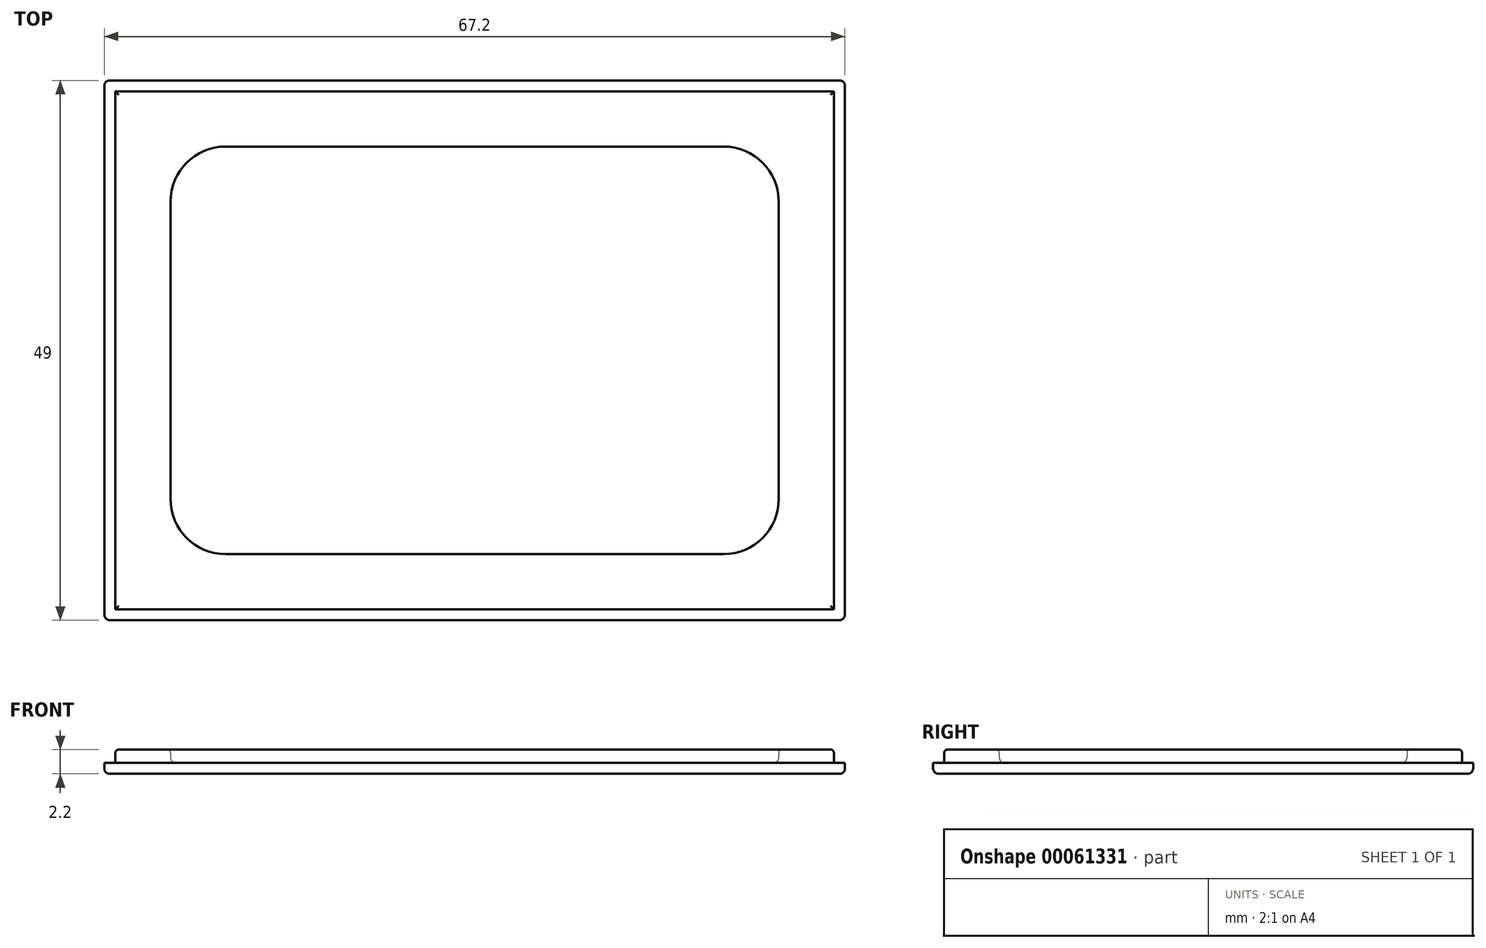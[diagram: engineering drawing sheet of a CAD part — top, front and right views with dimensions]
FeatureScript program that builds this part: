
annotation { "Feature Type Name" : "Feature", "Feature Type Description" : "" }
export const myFeature = defineFeature(function(context is Context, id is Id, definition is map)
    precondition{}
    {
        {
            var Q0;
            Q0=qCreatedBy(makeId("Top.planeOp"),FACE);
            var sketch = newSketch(context, id + "F0", { "sketchPlane" : qUnion([Q0])});
            skLineSegment(sketch, "E0.bottom", {"start": v(-25.22, 29.05) * mm, "end": v(41.98, 29.05) * mm});
            skLineSegment(sketch, "E0.top", {"start": v(-25.22, -19.95) * mm, "end": v(41.98, -19.95) * mm});
            skLineSegment(sketch, "E0.left", {"start": v(-25.22, 29.05) * mm, "end": v(-25.22, -19.95) * mm});
            skLineSegment(sketch, "E0.right", {"start": v(41.98, 29.05) * mm, "end": v(41.98, -19.95) * mm});
            skLineSegment(sketch, "E1.0", {"start": v(-24.22, 28.05) * mm, "end": v(40.98, 28.05) * mm});
            skLineSegment(sketch, "E1.1", {"start": v(-24.22, 28.05) * mm, "end": v(-24.22, -18.95) * mm});
            skLineSegment(sketch, "E1.2", {"start": v(-24.22, -18.95) * mm, "end": v(40.98, -18.95) * mm});
            skLineSegment(sketch, "E1.3", {"start": v(40.98, 28.05) * mm, "end": v(40.98, -18.95) * mm});
            skLineSegment(sketch, "E2.bottom", {"start": v(32.98, 28.05) * mm, "end": v(40.98, 28.05) * mm});
            skLineSegment(sketch, "E2.right", {"start": v(40.98, 28.05) * mm, "end": v(40.98, 20.05) * mm});
            skLineSegment(sketch, "E3.top", {"start": v(40.98, -18.95) * mm, "end": v(32.98, -18.95) * mm});
            skLineSegment(sketch, "E3.left", {"start": v(40.98, -10.95) * mm, "end": v(40.98, -18.95) * mm});
            skLineSegment(sketch, "E4.bottom", {"start": v(-16.22, 28.05) * mm, "end": v(-24.22, 28.05) * mm});
            skLineSegment(sketch, "E4.right", {"start": v(-24.22, 28.05) * mm, "end": v(-24.22, 20.05) * mm});
            skLineSegment(sketch, "E5.top", {"start": v(-24.22, -18.95) * mm, "end": v(-16.22, -18.95) * mm});
            skLineSegment(sketch, "E5.left", {"start": v(-24.22, -10.95) * mm, "end": v(-24.22, -18.95) * mm});
            skLineSegment(sketch, "E6.0", {"start": v(-14.22, 23.05) * mm, "end": v(30.98, 23.05) * mm});
            skLineSegment(sketch, "E7.0", {"start": v(35.98, 18.05) * mm, "end": v(35.98, -8.95) * mm});
            skLineSegment(sketch, "E7.1", {"start": v(-14.22, -13.95) * mm, "end": v(30.98, -13.95) * mm});
            skLineSegment(sketch, "E7.2", {"start": v(-19.22, 18.05) * mm, "end": v(-19.22, -8.95) * mm});
            skArc(sketch, "E8.filletArc", {"start": v(-14.22, 23.05) * mm, "mid": v(-17.76, 21.59) * mm, "end": v(-19.22, 18.05) * mm});
            skArc(sketch, "E9.filletArc", {"start": v(35.98, 18.05) * mm, "mid": v(34.51, 21.59) * mm, "end": v(30.98, 23.05) * mm});
            skPoint(sketch, "E10.visualSharp", {"position": v(-19.22, -13.95) * mm});
            skArc(sketch, "E10.filletArc", {"start": v(-19.22, -8.95) * mm, "mid": v(-17.76, -12.49) * mm, "end": v(-14.22, -13.95) * mm});
            skPoint(sketch, "E11.visualSharp", {"position": v(35.98, -13.95) * mm});
            skArc(sketch, "E11.filletArc", {"start": v(30.98, -13.95) * mm, "mid": v(34.51, -12.49) * mm, "end": v(35.98, -8.95) * mm});
            skSolve(sketch);
        }
        {
            var Q0;
            Q0=makeQuery(id+"F0.imprint","IMPRINT",FACE,{"disambiguationData":[TD([[makeQuery(id+"F0.imprint","IMPRINT",EDGE,{"derivedFrom":sQuery(id+"F0.wireOp",EDGE,"E6.0")}),-1.0]])]});
            var Q1;
            Q1=makeQuery(id+"F0.imprint","IMPRINT",FACE,{"disambiguationData":[TD([[makeQuery(id+"F0.imprint","IMPRINT",EDGE,{"derivedFrom":sQuery(id+"F0.wireOp",EDGE,"E0.bottom")}),-1.0]])]});
            var Q2;
            Q2=makeQuery(id+"F0.imprint","IMPRINT",FACE,{"disambiguationData":[TD([[makeQuery(id+"F0.imprint","IMPRINT",EDGE,{"derivedFrom":sQuery(id+"F0.wireOp",EDGE,"E1.0")}),-1.0]])]});
            extrude(context, id + "F1", {"entities" : qUnion([Q0, Q1, Q2]), "depth" : 1 * mm});
        }
        {
            var Q0;
            Q0=makeQuery(id+"F0.imprint","IMPRINT",FACE,{"disambiguationData":[TD([[makeQuery(id+"F0.imprint","IMPRINT",EDGE,{"derivedFrom":sQuery(id+"F0.wireOp",EDGE,"E1.0")}),-1.0]])]});
            extrude(context, id + "F2", {"entities" : qUnion([Q0]), "operationType" : NewBodyOperationType.ADD, "depth" : 2.2 * mm});
        }
        {
            var Q0;
            Q0=makeQuery(id+"F1.opExtrude","CAP_FACE",FACE,{"disambiguationData":[OSD([sQuery(id+"F0.wireOp",EDGE,"E0.bottom"),sQuery(id+"F0.wireOp",EDGE,"E0.top"),sQuery(id+"F0.wireOp",EDGE,"E0.left"),sQuery(id+"F0.wireOp",EDGE,"E0.right")])],"isStart":true});
            fillet(context, id + "F3", {"entities" : qUnion([Q0]), "radius" : 0.5 * mm, "tangentPropagation" : true, "allowEdgeOverflow" : false});
        }
        {
            var Q0;
            Q0=makeQuery(id+"F2.opExtrude","CAP_FACE",FACE,{"disambiguationData":[OSD([sQuery(id+"F0.wireOp",EDGE,"E1.0"),sQuery(id+"F0.wireOp",EDGE,"E1.1"),sQuery(id+"F0.wireOp",EDGE,"E1.2"),sQuery(id+"F0.wireOp",EDGE,"E1.3"),sQuery(id+"F0.wireOp",EDGE,"E2.bottom"),sQuery(id+"F0.wireOp",EDGE,"E2.right"),sQuery(id+"F0.wireOp",EDGE,"E3.top"),sQuery(id+"F0.wireOp",EDGE,"E3.left"),sQuery(id+"F0.wireOp",EDGE,"E4.bottom"),sQuery(id+"F0.wireOp",EDGE,"E4.right"),sQuery(id+"F0.wireOp",EDGE,"E5.top"),sQuery(id+"F0.wireOp",EDGE,"E5.left"),sQuery(id+"F0.wireOp",EDGE,"E6.0"),sQuery(id+"F0.wireOp",EDGE,"E7.0"),sQuery(id+"F0.wireOp",EDGE,"E7.1"),sQuery(id+"F0.wireOp",EDGE,"E7.2"),sQuery(id+"F0.wireOp",EDGE,"E8.filletArc"),sQuery(id+"F0.wireOp",EDGE,"E9.filletArc"),sQuery(id+"F0.wireOp",EDGE,"E10.filletArc"),sQuery(id+"F0.wireOp",EDGE,"E11.filletArc")])],"isStart":false});
            fillet(context, id + "F4", {"entities" : qUnion([Q0]), "radius" : 0.3 * mm, "tangentPropagation" : true, "allowEdgeOverflow" : false});
        }
        {
            var Q0;
            Q0=makeQuery(id+"F2.opExtrude","SWEPT_EDGE",EDGE,{"disambiguationData":[OSD([sQuery(id+"F0.wireOp",EDGE,"E2.bottom"),sQuery(id+"F0.wireOp",EDGE,"E2.right")])]});
            var Q1;
            Q1=makeQuery(id+"F1.opExtrude","SWEPT_EDGE",EDGE,{"disambiguationData":[OSD([sQuery(id+"F0.wireOp",EDGE,"E0.bottom"),sQuery(id+"F0.wireOp",EDGE,"E0.right")])]});
            var Q2;
            Q2=makeQuery(id+"F2.opExtrude","SWEPT_EDGE",EDGE,{"disambiguationData":[OSD([sQuery(id+"F0.wireOp",EDGE,"E3.top"),sQuery(id+"F0.wireOp",EDGE,"E3.left")])]});
            var Q3;
            Q3=makeQuery(id+"F1.opExtrude","SWEPT_EDGE",EDGE,{"disambiguationData":[OSD([sQuery(id+"F0.wireOp",EDGE,"E0.top"),sQuery(id+"F0.wireOp",EDGE,"E0.right")])]});
            var Q4;
            Q4=makeQuery(id+"F2.opExtrude","SWEPT_EDGE",EDGE,{"disambiguationData":[OSD([sQuery(id+"F0.wireOp",EDGE,"E5.top"),sQuery(id+"F0.wireOp",EDGE,"E5.left")])]});
            var Q5;
            Q5=makeQuery(id+"F1.opExtrude","SWEPT_EDGE",EDGE,{"disambiguationData":[OSD([sQuery(id+"F0.wireOp",EDGE,"E0.top"),sQuery(id+"F0.wireOp",EDGE,"E0.left")])]});
            var Q6;
            Q6=makeQuery(id+"F2.opExtrude","SWEPT_EDGE",EDGE,{"disambiguationData":[OSD([sQuery(id+"F0.wireOp",EDGE,"E4.bottom"),sQuery(id+"F0.wireOp",EDGE,"E4.right")])]});
            var Q7;
            Q7=makeQuery(id+"F1.opExtrude","SWEPT_EDGE",EDGE,{"disambiguationData":[OSD([sQuery(id+"F0.wireOp",EDGE,"E0.bottom"),sQuery(id+"F0.wireOp",EDGE,"E0.left")])]});
            fillet(context, id + "F5", {"entities" : qUnion([Q0, Q1, Q2, Q3, Q4, Q5, Q6, Q7]), "radius" : 0.5 * mm, "tangentPropagation" : true, "allowEdgeOverflow" : false});
        }
        {
            var Q0;
            Q0=makeQuery(id+"F2.boolean.opBoolean","SPLIT",FACE,{"disambiguationData":[TD([makeQuery(id+"F2.opExtrude","SWEPT_FACE",FACE,{"disambiguationData":[OSD([sQuery(id+"F0.wireOp",EDGE,"E6.0")])]})])],"derivedFrom":makeQuery(id+"F1.opExtrude","CAP_FACE",FACE,{"disambiguationData":[OSD([sQuery(id+"F0.wireOp",EDGE,"E0.bottom"),sQuery(id+"F0.wireOp",EDGE,"E0.top"),sQuery(id+"F0.wireOp",EDGE,"E0.left"),sQuery(id+"F0.wireOp",EDGE,"E0.right")])],"isStart":false})});
            fillet(context, id + "F6", {"entities" : qUnion([Q0]), "radius" : 0.5 * mm, "tangentPropagation" : true, "allowEdgeOverflow" : false});
        }
    });
